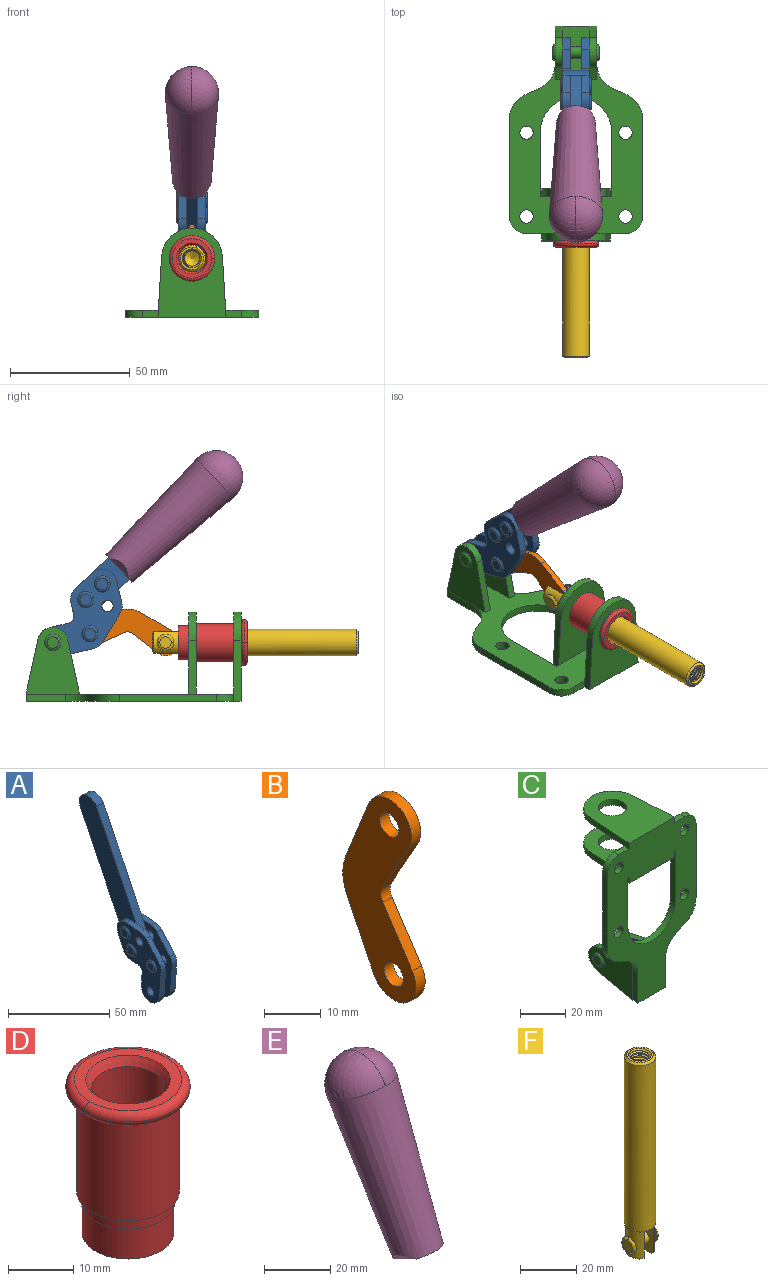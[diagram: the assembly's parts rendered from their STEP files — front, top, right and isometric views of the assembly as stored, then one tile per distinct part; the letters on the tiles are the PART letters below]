
ASSEMBLY  parts=6 mates=6
PART A: 59 faces, bbox 12.9x60.2x99.6 mm
  f0: torus R=2.39mm, axis (-1,0,0), area 14.9mm2, adj f20,f43,f51
  f1: torus R=2.39mm, axis (-1,0,0), area 14.9mm2, adj f19,f42,f51
  f2: torus R=2.39mm, axis (-1,0,0), area 14.9mm2, adj f18,f35,f51
  f3: torus R=2.39mm, axis (-1,0,0), area 14.9mm2, adj f14,f17,f23
  f4: torus R=2.39mm, axis (-1,0,0), area 14.9mm2, adj f13,f16,f23
  f5: torus R=2.39mm, axis (-1,0,0), area 14.9mm2, adj f12,f15,f23
  f6: cylinder r=2.39mm len=4.78mm, axis (1,0,0), area 46.5mm2, adj f48,f50,f51
  f7: cylinder r=2.39mm len=4.78mm, axis (1,0,0), area 46.5mm2, adj f50,f51
  f8: cylinder r=6.35mm len=12.68mm, axis (1,0,0), area 61.8mm2, adj f38,f39,f50,f51
  f9: cylinder r=2.39mm len=4.78mm, axis (-1,0,0), area 70.5mm2, adj f46,f50
  f10: cylinder r=2.39mm len=4.78mm, axis (-1,0,0), area 46.5mm2, adj f23,f45,f46
  f11: cylinder r=2.39mm len=4.78mm, axis (-1,0,0), area 46.5mm2, adj f23,f46
  f12: plane 4.78x4.78mm, normal (1,0,0), area 17.9mm2, adj f5,f15
  f13: plane 4.78x4.78mm, normal (1,0,0), area 17.9mm2, adj f4,f16
  f14: plane 4.78x4.78mm, normal (1,0,0), area 17.9mm2, adj f3,f17
  f15: torus R=2.39mm, axis (-1,0,0), area 14.9mm2, adj f5,f12,f23
  f16: torus R=2.39mm, axis (-1,0,0), area 14.9mm2, adj f4,f13,f23
  f17: torus R=2.39mm, axis (-1,0,0), area 14.9mm2, adj f3,f14,f23
  f18: plane 4.78x4.78mm, normal (-1,0,0), area 17.9mm2, adj f2,f35
  f19: plane 4.78x4.78mm, normal (-1,0,0), area 17.9mm2, adj f1,f42
  f20: plane 4.78x4.78mm, normal (-1,0,0), area 17.9mm2, adj f0,f43
  f21: plane 2.26x0.2mm, normal (1,0,0), area 0.2mm2, adj f31,f44
  f22: plane 2.26x0.2mm, normal (-1,0,0), area 0.2mm2, adj f41,f44
  f23: plane 39.37x30.77mm, normal (1,0,0), area 565.5mm2, adj f3,f4,f5,f10,f11,f15,f16,f17
  f24: cylinder r=6.1mm len=4.15mm, axis (-1,0,0), area 14.7mm2, adj f23,f25,f32,f46
  f25: plane 10.25x9.01mm, normal (0,-0.75,0.66), area 42.3mm2, adj f23,f24,f26,f46
  f26: cylinder r=6.35mm len=4.64mm, axis (-1,0,0), area 15.6mm2, adj f23,f25,f27,f46
  f27: plane 15.84x3.1mm, normal (0,-1,-0.07), area 49.2mm2, adj f23,f26,f28,f46
  f28: cylinder r=6.35mm len=12.68mm, axis (-1,0,0), area 61.8mm2, adj f23,f27,f29,f46
  f29: plane 8.11x3.1mm, normal (0,1,0.07), area 25.2mm2, adj f23,f28,f30,f46
  f30: cylinder r=3.05mm len=3.25mm, axis (-1,0,0), area 14.8mm2, adj f23,f29,f31,f46
  f31: plane 5.99x3.1mm, normal (0,0.07,-1), area 18.6mm2, adj f21,f23,f30,f44,f46
  f32: plane 9.5x3.1mm, normal (0,-0.07,1), area 29.5mm2, adj f23,f24,f33,f46,f47
  f33: cylinder r=6.1mm len=8.63mm, axis (-1,0,0), area 39.1mm2, adj f23,f32,f34,f47
  f34: plane 8.65x3.96mm, normal (0,0.91,-0.42), area 29.5mm2, adj f23,f33,f44,f47
  f35: torus R=2.39mm, axis (-1,0,0), area 14.9mm2, adj f2,f18,f51
  f36: plane 10.25x9.01mm, normal (0,-0.75,0.66), area 42.3mm2, adj f37,f49,f50,f51
  f37: cylinder r=6.35mm len=4.64mm, axis (1,0,0), area 15.6mm2, adj f36,f38,f50,f51
  f38: plane 15.84x3.1mm, normal (0,-1,-0.07), area 49.2mm2, adj f8,f37,f50,f51
  f39: plane 8.11x3.1mm, normal (0,1,0.07), area 25.2mm2, adj f8,f40,f50,f51
  f40: cylinder r=3.05mm len=3.25mm, axis (1,0,0), area 14.8mm2, adj f39,f41,f50,f51
  f41: plane 5.99x3.1mm, normal (0,0.07,-1), area 18.6mm2, adj f22,f40,f44,f50,f51
  f42: torus R=2.39mm, axis (-1,0,0), area 14.9mm2, adj f1,f19,f51
  f43: torus R=2.39mm, axis (-1,0,0), area 14.9mm2, adj f0,f20,f51
  f44: cylinder r=6.35mm len=12.12mm, axis (-1,0,0), area 128.9mm2, adj f21,f22,f23,f31,f34,f41,f46,f47
  f45: plane 2.65x1.35mm, normal (1,0,0), area 1mm2, adj f10,f55
  f46: plane 39.08x20.42mm, normal (-1,0,0), area 412.5mm2, adj f9,f10,f11,f24,f25,f26,f27,f28
  f47: plane 77.62x39.82mm, normal (1,0,0), area 850mm2, adj f32,f33,f34,f44,f53,f54,f55
  f48: plane 2.65x1.35mm, normal (-1,0,0), area 1mm2, adj f6,f55
  f49: cylinder r=6.1mm len=4.15mm, axis (1,0,0), area 14.7mm2, adj f36,f50,f51,f56
  f50: plane 39.08x20.42mm, normal (1,0,0), area 412.5mm2, adj f6,f7,f8,f9,f36,f37,f38,f39
  f51: plane 39.37x30.77mm, normal (-1,0,0), area 565.5mm2, adj f0,f1,f2,f6,f7,f8,f35,f36
  f52: plane 8.65x3.96mm, normal (0,0.91,-0.42), area 29.5mm2, adj f44,f51,f57,f58
  f53: plane 68.49x33.4mm, normal (0,0.9,-0.44), area 358.1mm2, adj f44,f47,f54,f58
  f54: cylinder r=6.35mm len=12.06mm, axis (1,0,0), area 93.7mm2, adj f47,f53,f55,f58
  f55: plane 68.49x33.4mm, normal (0,-0.9,0.44), area 358.1mm2, adj f44,f45,f46,f47,f48,f50,f54,f58
  f56: plane 9.5x3.1mm, normal (0,-0.07,1), area 29.5mm2, adj f49,f50,f51,f57,f58
  f57: cylinder r=6.1mm len=8.63mm, axis (1,0,0), area 39.1mm2, adj f51,f52,f56,f58
  f58: plane 77.62x39.82mm, normal (-1,0,0), area 850mm2, adj f44,f52,f53,f54,f55,f56,f57
PART B: 12 faces, bbox 2.3x18.2x42.8 mm
  f0: cylinder r=2.4mm len=4.8mm, axis (1,0,0), area 34.9mm2, adj f4,f11
  f1: cylinder r=10.41mm len=8.47mm, axis (1,0,0), area 20.2mm2, adj f4,f9,f10,f11
  f2: cylinder r=3.05mm len=3.16mm, axis (1,0,0), area 7.7mm2, adj f4,f6,f7,f11
  f3: cylinder r=2.4mm len=4.8mm, axis (1,0,0), area 34.9mm2, adj f4,f11
  f4: plane 42.81x18.23mm, normal (-1,0,0), area 414.1mm2, adj f0,f1,f2,f3,f5,f6,f7,f8
  f5: cylinder r=5.54mm len=10.67mm, axis (1,0,0), area 41.8mm2, adj f4,f6,f10,f11
  f6: plane 11.66x6.53mm, normal (0,-0.87,-0.49), area 30.9mm2, adj f2,f4,f5,f11
  f7: plane 11.17x7.33mm, normal (0,-0.84,0.55), area 30.9mm2, adj f2,f4,f8,f11
  f8: cylinder r=5.54mm len=10.51mm, axis (1,0,0), area 41.8mm2, adj f4,f7,f9,f11
  f9: plane 13.67x6.67mm, normal (0,0.9,-0.44), area 35.1mm2, adj f1,f4,f8,f11
  f10: plane 14.1x5.7mm, normal (0,0.93,0.37), area 35.1mm2, adj f1,f4,f5,f11
  f11: plane 42.81x18.23mm, normal (1,0,0), area 414.1mm2, adj f0,f1,f2,f3,f5,f6,f7,f8
PART C: 55 faces, bbox 55.7x37.4x89.8 mm
  f0: torus R=2.41mm, axis (-1,0,0), area 15mm2, adj f11,f15,f25
  f1: torus R=2.41mm, axis (-1,0,0), area 15mm2, adj f10,f12,f22
  f2: cylinder r=2.78mm len=5.56mm, axis (0,-1,0), area 54.2mm2, adj f30,f54
  f3: cylinder r=14.99mm len=29.97mm, axis (0,-1,0), area 145.9mm2, adj f30,f49,f53,f54
  f4: cylinder r=2.78mm len=5.56mm, axis (0,-1,0), area 54.2mm2, adj f30,f54
  f5: cylinder r=2.78mm len=5.56mm, axis (0,-1,0), area 54.2mm2, adj f30,f54
  f6: cylinder r=2.78mm len=5.56mm, axis (0,-1,0), area 54.2mm2, adj f30,f54
  f7: cylinder r=6.35mm len=12.7mm, axis (0,0,1), area 123.6mm2, adj f27,f51
  f8: cylinder r=6.35mm len=12.7mm, axis (0,0,-1), area 124.7mm2, adj f21,f35
  f9: cylinder r=2.41mm len=11.18mm, axis (-1,0,0), area 169.4mm2, adj f16,f19
  f10: plane 4.83x4.83mm, normal (1,0,0), area 18.3mm2, adj f1,f12
  f11: plane 4.83x4.83mm, normal (-1,0,0), area 18.3mm2, adj f0,f15
  f12: torus R=2.41mm, axis (-1,0,0), area 15mm2, adj f1,f10,f22
  f13: cylinder r=6.35mm len=12.41mm, axis (1,0,0), area 53.4mm2, adj f18,f19,f22,f23
  f14: cylinder r=6.35mm len=12.41mm, axis (-1,0,0), area 53.4mm2, adj f16,f17,f24,f25
  f15: torus R=2.41mm, axis (-1,0,0), area 15mm2, adj f0,f11,f25
  f16: plane 27.86x22.35mm, normal (1,0,0), area 425.4mm2, adj f9,f14,f17,f24,f30
  f17: plane 22.86x4.97mm, normal (0,0.21,0.98), area 72.5mm2, adj f14,f16,f25,f30
  f18: plane 22.86x4.97mm, normal (0,0.21,0.98), area 72.5mm2, adj f13,f19,f22,f30
  f19: plane 27.86x22.35mm, normal (-1,0,0), area 425.4mm2, adj f9,f13,f18,f23,f30
  f20: cylinder r=12.7mm len=25.35mm, axis (0,0,-1), area 119.8mm2, adj f21,f34,f35,f36
  f21: plane 34.21x28.07mm, normal (0,0,-1), area 702.4mm2, adj f8,f20,f30,f34,f36
  f22: plane 27.96x22.45mm, normal (1,0,0), area 407.2mm2, adj f1,f12,f13,f18,f23,f30,f42,f43
  f23: plane 22.86x4.97mm, normal (0,0.21,-0.98), area 72.5mm2, adj f13,f19,f22,f44
  f24: plane 22.86x4.97mm, normal (0,0.21,-0.98), area 72.5mm2, adj f14,f16,f25,f44
  f25: plane 27.86x22.35mm, normal (-1,0,0), area 407.1mm2, adj f0,f14,f15,f17,f24,f30,f45,f46
  f26: plane 3.1x0.95mm, normal (0,0,-1), area 2.7mm2, adj f30,f49,f50,f54
  f27: plane 34.21x28.07mm, normal (0,0,1), area 702.4mm2, adj f7,f28,f30,f50,f52
  f28: cylinder r=12.7mm len=25.35mm, axis (0,0,1), area 118.8mm2, adj f27,f50,f51,f52
  f29: plane 3.1x0.95mm, normal (0,0,-1), area 2.7mm2, adj f30,f52,f53,f54
  f30: plane 86.54x55.63mm, normal (0,1,0), area 2362.9mm2, adj f2,f3,f4,f5,f6,f16,f17,f18
  f31: plane 40.56x3.1mm, normal (-1,0,0), area 125.7mm2, adj f30,f32,f48,f54
  f32: cylinder r=7.11mm len=7.11mm, axis (0,-1,0), area 34.6mm2, adj f30,f31,f33,f54
  f33: plane 6.67x3.1mm, normal (0,0,1), area 20.4mm2, adj f30,f32,f34,f54
  f34: plane 25.39x3.13mm, normal (-1,0.06,0), area 79.5mm2, adj f20,f21,f33,f35,f54
  f35: plane 37.31x28.45mm, normal (0,0,1), area 789.9mm2, adj f8,f20,f34,f36,f54
  f36: plane 25.39x3.13mm, normal (1,0.06,0), area 79.5mm2, adj f20,f21,f35,f37,f54
  f37: plane 6.67x3.1mm, normal (0,0,1), area 20.4mm2, adj f30,f36,f38,f54
  f38: cylinder r=7.11mm len=7.11mm, axis (0,-1,0), area 34.6mm2, adj f30,f37,f39,f54
  f39: plane 40.56x3.1mm, normal (1,0,0), area 125.7mm2, adj f30,f38,f40,f54
  f40: cylinder r=11.18mm len=10.16mm, axis (0,-1,0), area 39.5mm2, adj f30,f39,f41,f54
  f41: plane 6.09x3.1mm, normal (0.42,0,-0.91), area 20.8mm2, adj f30,f40,f42,f54
  f42: cylinder r=11.18mm len=9.41mm, axis (0,-1,0), area 37.2mm2, adj f22,f30,f41,f43,f54
  f43: plane 16.5x3.1mm, normal (1,0,0), area 51.1mm2, adj f22,f42,f44,f54
  f44: plane 17.37x3.1mm, normal (0,0,-1), area 53.8mm2, adj f23,f24,f30,f43,f45,f54
  f45: plane 16.5x3.1mm, normal (-1,0,0), area 51.1mm2, adj f25,f44,f46,f54
  f46: cylinder r=11.18mm len=9.41mm, axis (0,-1,0), area 37.2mm2, adj f25,f30,f45,f47,f54
  f47: plane 6.09x3.1mm, normal (-0.42,0,-0.91), area 20.8mm2, adj f30,f46,f48,f54
  f48: cylinder r=11.18mm len=10.16mm, axis (0,-1,0), area 39.5mm2, adj f30,f31,f47,f54
  f49: plane 26.54x3.1mm, normal (-1,0,0), area 82.3mm2, adj f3,f26,f30,f54
  f50: plane 25.39x3.1mm, normal (1,0.06,0), area 78.8mm2, adj f26,f27,f28,f51,f54
  f51: plane 37.31x28.45mm, normal (0,0,-1), area 789.9mm2, adj f7,f28,f50,f52,f54
  f52: plane 25.39x3.1mm, normal (-1,0.06,0), area 78.8mm2, adj f27,f28,f29,f51,f54
  f53: plane 26.54x3.1mm, normal (1,0,0), area 82.3mm2, adj f3,f29,f30,f54
  f54: plane 89.66x55.63mm, normal (0,-1,0), area 2678.5mm2, adj f2,f3,f4,f5,f6,f26,f29,f31
PART D: 15 faces, bbox 20.6x20.6x28.7 mm
  f0: torus R=8.26mm, axis (0,0,1), area 56.8mm2, adj f1,f10,f12
  f1: torus R=8.26mm, axis (0,0,1), area 56.8mm2, adj f0,f6,f13
  f2: cylinder r=5.59mm len=25.91mm, axis (0,0,1), area 909.6mm2, adj f3,f4
  f3: cone r=6.86mm half-angle=45deg, axis (0,0,-1), area 70.2mm2, adj f2,f14
  f4: cone r=6.47mm half-angle=30deg, axis (0,0,1), area 66.7mm2, adj f2,f13
  f5: cylinder r=7.04mm len=14.07mm, axis (0,0,1), area 252.6mm2, adj f11,f14
  f6: torus R=8.26mm, axis (0,0,1), area 56.8mm2, adj f1,f12,f13
  f7: cylinder r=7.16mm len=14.33mm, axis (0,0,1), area 91.5mm2, adj f9,f11
  f8: cylinder r=7.86mm len=18.42mm, axis (0,0,1), area 909.6mm2, adj f9,f10
  f9: plane 15.72x15.72mm, normal (0,0,-1), area 33mm2, adj f7,f8
  f10: plane 16.51x16.51mm, normal (0,0,-1), area 19.9mm2, adj f0,f8,f12
  f11: plane 14.33x14.33mm, normal (0,0,-1), area 5.7mm2, adj f5,f7
  f12: torus R=8.26mm, axis (0,0,1), area 56.8mm2, adj f0,f6,f10
  f13: plane 16.51x16.51mm, normal (0,0,1), area 82.7mm2, adj f1,f4,f6
  f14: plane 14.07x14.07mm, normal (0,0,-1), area 7.8mm2, adj f3,f5
PART E: 11 faces, bbox 22.3x42.6x64.5 mm
  f0: sphere r=11.13mm, area 411.4mm2, adj f1,f8
  f1: cone r=11.11mm half-angle=3.3deg, axis (0,0.44,0.9), area 3251.8mm2, adj f0,f7,f8,f9,f10
  f2: cylinder r=6.16mm len=11.7mm, axis (1,0,0), area 89.5mm2, adj f3,f4,f5,f6
  f3: plane 60.23x36.75mm, normal (-1,0,0), area 763.6mm2, adj f2,f4,f6,f10
  f4: plane 51.37x25.05mm, normal (0,0.9,-0.44), area 264.2mm2, adj f2,f3,f5,f10
  f5: plane 60.23x36.75mm, normal (1,0,0), area 763.6mm2, adj f2,f4,f6,f10
  f6: plane 51.37x25.05mm, normal (0,-0.9,0.44), area 264.2mm2, adj f2,f3,f5,f10
  f7: plane 9.95x5.95mm, normal (0.71,-0.31,-0.64), area 25.8mm2, adj f1,f10
  f8: sphere r=11.13mm, area 411.4mm2, adj f0,f1
  f9: plane 9.95x5.95mm, normal (-0.71,-0.31,-0.64), area 25.8mm2, adj f1,f10
  f10: plane 14.27x11.38mm, normal (0,-0.44,-0.9), area 106.7mm2, adj f1,f3,f4,f5,f6,f7,f9
PART F: 48 faces, bbox 12.6x11.1x86.1 mm
  f0: torus R=2.41mm, axis (-1,0,0), area 15mm2, adj f30,f32,f34
  f1: torus R=2.41mm, axis (-1,0,0), area 15mm2, adj f29,f31,f33
  f2: cylinder r=5.54mm len=72.39mm, axis (0,0,1), area 2518.5mm2, adj f3,f4,f42,f43
  f3: cone r=5.54mm half-angle=45deg, axis (0,0,1), area 7.6mm2, adj f2,f5,f41
  f4: cone r=5.54mm half-angle=45deg, axis (0,0,-1), area 34.9mm2, adj f2,f39
  f5: cylinder r=5.08mm len=11.48mm, axis (0,0,1), area 108.3mm2, adj f3,f7,f8,f41
  f6: cylinder r=2.41mm len=4.83mm, axis (-1,0,0), area 71.2mm2, adj f40,f41
  f7: cylinder r=2.41mm len=4.83mm, axis (-1,0,0), area 7.6mm2, adj f5,f34
  f8: cone r=5.08mm half-angle=45deg, axis (0,0,1), area 10.6mm2, adj f5,f37,f41
  f9: cone r=3.98mm half-angle=45deg, axis (0,0,1), area 17.6mm2, adj f27,f39,f45,f46,f47
  f10: cylinder r=2.41mm len=4.83mm, axis (-1,0,0), area 7.6mm2, adj f33,f38
  f11: cylinder r=3.2mm len=6.4mm, axis (0,0,1), area 78.4mm2, adj f12,f28,f44,f45,f47
  f12: cylinder r=3.2mm len=6.4mm, axis (0,0,1), area 10.5mm2, adj f11,f13,f45,f47
  f13: cylinder r=3.2mm len=6.4mm, axis (0,0,1), area 10.5mm2, adj f12,f14,f45,f47
  f14: cylinder r=3.2mm len=6.4mm, axis (0,0,1), area 10.5mm2, adj f13,f15,f45,f47
  f15: cylinder r=3.2mm len=6.4mm, axis (0,0,1), area 10.5mm2, adj f14,f16,f45,f47
  f16: cylinder r=3.2mm len=6.4mm, axis (0,0,1), area 10.5mm2, adj f15,f17,f45,f47
  f17: cylinder r=3.2mm len=6.4mm, axis (0,0,1), area 10.5mm2, adj f16,f18,f45,f47
  f18: cylinder r=3.2mm len=6.4mm, axis (0,0,1), area 10.5mm2, adj f17,f19,f45,f47
  f19: cylinder r=3.2mm len=6.4mm, axis (0,0,1), area 10.5mm2, adj f18,f20,f45,f47
  f20: cylinder r=3.2mm len=6.4mm, axis (0,0,1), area 10.5mm2, adj f19,f21,f45,f47
  f21: cylinder r=3.2mm len=6.4mm, axis (0,0,1), area 10.5mm2, adj f20,f22,f45,f47
  f22: cylinder r=3.2mm len=6.4mm, axis (0,0,1), area 10.5mm2, adj f21,f23,f45,f47
  f23: cylinder r=3.2mm len=6.4mm, axis (0,0,1), area 10.5mm2, adj f22,f24,f45,f47
  f24: cylinder r=3.2mm len=6.4mm, axis (0,0,1), area 10.5mm2, adj f23,f25,f45,f47
  f25: cylinder r=3.2mm len=6.4mm, axis (0,0,1), area 10.5mm2, adj f24,f26,f45,f47
  f26: cylinder r=3.2mm len=6.4mm, axis (0,0,1), area 10.5mm2, adj f25,f27,f45,f47
  f27: cylinder r=3.2mm len=6.4mm, axis (0,0,1), area 7.4mm2, adj f9,f26,f45,f47
  f28: cone r=3.2mm half-angle=60deg, axis (0,0,1), area 37.2mm2, adj f11
  f29: plane 4.83x4.83mm, normal (-1,0,0), area 18.3mm2, adj f1,f31
  f30: plane 4.83x4.83mm, normal (1,0,0), area 18.3mm2, adj f0,f32
  f31: torus R=2.41mm, axis (-1,0,0), area 15mm2, adj f1,f29,f33
  f32: torus R=2.41mm, axis (-1,0,0), area 15mm2, adj f0,f30,f34
  f33: plane 6.83x6.83mm, normal (1,0,0), area 18.3mm2, adj f1,f10,f31
  f34: plane 6.83x6.83mm, normal (-1,0,0), area 18.3mm2, adj f0,f7,f32
  f35: cone r=5.08mm half-angle=45deg, axis (0,0,1), area 10.6mm2, adj f36,f38,f40
  f36: plane 7.25x1.97mm, normal (0,0,-1), area 10mm2, adj f35,f40
  f37: plane 7.25x1.97mm, normal (0,0,-1), area 10mm2, adj f8,f41
  f38: cylinder r=5.08mm len=11.48mm, axis (0,0,1), area 108.3mm2, adj f10,f35,f40,f42
  f39: plane 9.55x9.55mm, normal (0,0,1), area 22mm2, adj f4,f9
  f40: plane 12.76x10.09mm, normal (1,0,0), area 95.7mm2, adj f6,f35,f36,f38,f42,f43
  f41: plane 12.76x10.09mm, normal (-1,0,0), area 95.7mm2, adj f3,f5,f6,f8,f37,f43
  f42: cone r=5.54mm half-angle=45deg, axis (0,0,1), area 7.6mm2, adj f2,f38,f40
  f43: plane 11.07x4.7mm, normal (0,0,-1), area 50.4mm2, adj f2,f40,f41
  f44: plane 0.89x0.62mm, normal (-1,0,0), area 0.3mm2, adj f11,f45,f46,f47
  f45: bspline ~24.8x7.63mm, area 266.6mm2, adj f9,f11,f12,f13,f14,f15,f16,f17
  f46: bspline ~24.87x7.63mm, area 73.6mm2, adj f9,f44,f45,f47
  f47: bspline ~24.98x7.63mm, area 272.5mm2, adj f9,f11,f12,f13,f14,f15,f16,f17
PLACE A rot(axis=(1,0,0),72.8deg) t=(0,3.59,10.58)mm
PLACE B rot(axis=(1,0,0),98.5deg) t=(0,13.48,2.57)mm
PLACE C rot(axis=(1,0,0),90deg) t=(0,9.43,0)mm fixed
PLACE D rot(axis=(1,0,0),90deg) t=(0,9.43,0)mm
PLACE E rot(axis=(1,0,0),72.8deg) t=(-0.04,3.59,10.58)mm
PLACE F rot(axis=(1,0,0),90deg) t=(0,10,0)mm
MATE revolute B.f3 <-> A.f4  axis (1,0,0) through (0,26.07,28.23)mm
MATE fastened D.f2 <-> C.f7  axis (0,1,0) through (0,-36.96,24.61)mm
MATE revolute A.f7 <-> C.f0  axis (-1,0,0) through (0,41.52,24.61)mm
MATE slider F.f2 <-> D.f2  axis (0,-1,0) through (0,-48.78,24.61)mm
MATE fastened E.f2 <-> A.f54  axis (1,0,0) through (-2.35,-27.75,94.63)mm
MATE revolute B.f5 <-> F.f6  axis (1,0,0) through (0,-5.48,24.61)mm
